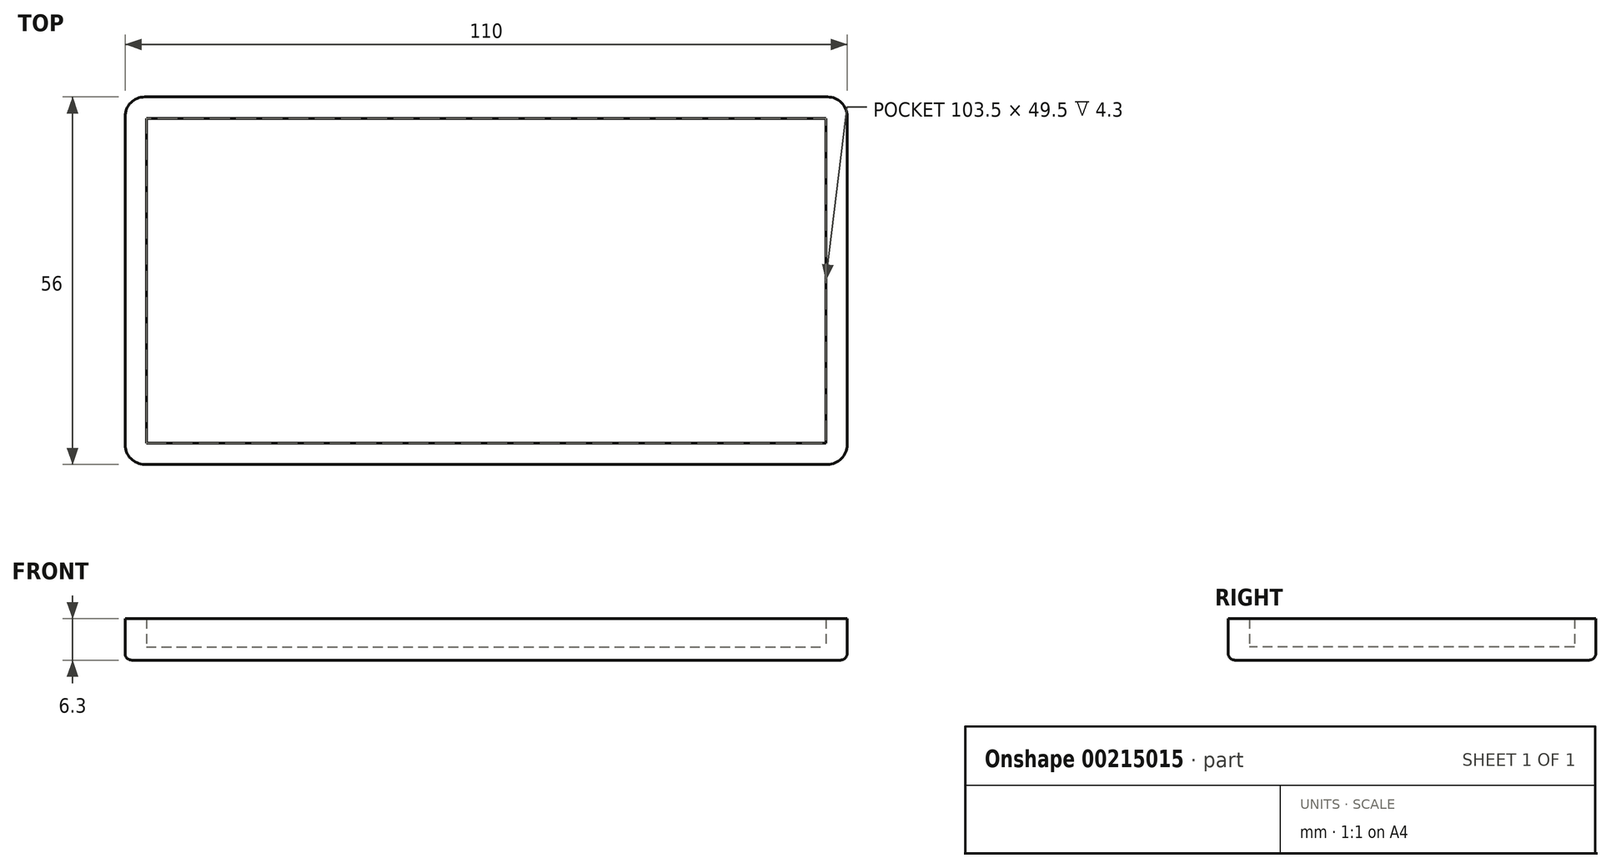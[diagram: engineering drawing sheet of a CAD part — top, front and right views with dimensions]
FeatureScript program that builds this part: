
annotation { "Feature Type Name" : "Feature", "Feature Type Description" : "" }
export const myFeature = defineFeature(function(context is Context, id is Id, definition is map)
    precondition{}
    {
        {
            assignVariable(context, id + "F0", {"name" : "SpessorePiano", "anyValue" : 2 * mm});
        }
        {
            assignVariable(context, id + "F1", {"name" : "AltezzaBordi", "anyValue" : 4.3 * mm});
        }
        {
            assignVariable(context, id + "F2", {"name" : "RaggiaturaSpigoli", "anyValue" : 3 * mm});
        }
        {
            assignVariable(context, id + "F3", {"name" : "RaggiaturaFacciaPiano", "anyValue" : 1 * mm});
        }
        {
            var Q0;
            Q0=qCreatedBy(makeId("Top.planeOp"),FACE);
            var sketch = newSketch(context, id + "F4", { "sketchPlane" : qUnion([Q0])});
            skLineSegment(sketch, "E0.bottom", {"start": v(-51.75, 24.75) * mm, "end": v(51.75, 24.75) * mm});
            skLineSegment(sketch, "E0.top", {"start": v(-51.75, -24.75) * mm, "end": v(51.75, -24.75) * mm});
            skLineSegment(sketch, "E0.left", {"start": v(-51.75, 24.75) * mm, "end": v(-51.75, -24.75) * mm});
            skLineSegment(sketch, "E0.right", {"start": v(51.75, 24.75) * mm, "end": v(51.75, -24.75) * mm});
            skPoint(sketch, "E0.middle", {"position": v(0, 0) * mm});
            skLineSegment(sketch, "E1.bottom", {"start": v(-55, 28) * mm, "end": v(55, 28) * mm});
            skLineSegment(sketch, "E1.top", {"start": v(-55, -28) * mm, "end": v(55, -28) * mm});
            skLineSegment(sketch, "E1.left", {"start": v(-55, 28) * mm, "end": v(-55, -28) * mm});
            skLineSegment(sketch, "E1.right", {"start": v(55, 28) * mm, "end": v(55, -28) * mm});
            skSolve(sketch);
        }
        {
            var Q0;
            Q0 = qSketchRegion(id + "F4", true);
            var Q1;
            Q1=makeQuery(id+"F4.imprint","IMPRINT",FACE,{"disambiguationData":[TD([[makeQuery(id+"F4.imprint","IMPRINT",EDGE,{"derivedFrom":sQuery(id+"F4.wireOp",EDGE,"E0.bottom")}),-1.0]])]});
            extrude(context, id + "F5", {"entities" : qUnion([Q0, Q1]), "oppositeDirection" : true, "depth" : getVariable(context, 'SpessorePiano')});
        }
        {
            var Q0;
            Q0 = qSketchRegion(id + "F4", true);
            extrude(context, id + "F6", {"entities" : qUnion([Q0]), "operationType" : NewBodyOperationType.ADD, "depth" : getVariable(context, 'AltezzaBordi')});
        }
        {
            var Q0;
            {var subQ0=sQuery(id+"F4.wireOp",EDGE,"E1.left");var subQ1=sQuery(id+"F4.wireOp",EDGE,"E1.top");Q0=makeQuery(id+"F6.boolean.opBoolean","MERGE",EDGE,{"derivedFrom":[makeQuery(id+"F5.opExtrude","SWEPT_EDGE",EDGE,{"disambiguationData":[OSD([subQ1,subQ0])]}),makeQuery(id+"F6.opExtrude","SWEPT_EDGE",EDGE,{"disambiguationData":[OSD([subQ1,subQ0])]})]});}
            var Q1;
            {var subQ0=sQuery(id+"F4.wireOp",EDGE,"E1.right");var subQ1=sQuery(id+"F4.wireOp",EDGE,"E1.top");Q1=makeQuery(id+"F6.boolean.opBoolean","MERGE",EDGE,{"derivedFrom":[makeQuery(id+"F5.opExtrude","SWEPT_EDGE",EDGE,{"disambiguationData":[OSD([subQ1,subQ0])]}),makeQuery(id+"F6.opExtrude","SWEPT_EDGE",EDGE,{"disambiguationData":[OSD([subQ1,subQ0])]})]});}
            var Q2;
            {var subQ0=sQuery(id+"F4.wireOp",EDGE,"E1.right");var subQ1=sQuery(id+"F4.wireOp",EDGE,"E1.bottom");Q2=makeQuery(id+"F6.boolean.opBoolean","MERGE",EDGE,{"derivedFrom":[makeQuery(id+"F5.opExtrude","SWEPT_EDGE",EDGE,{"disambiguationData":[OSD([subQ1,subQ0])]}),makeQuery(id+"F6.opExtrude","SWEPT_EDGE",EDGE,{"disambiguationData":[OSD([subQ1,subQ0])]})]});}
            var Q3;
            {var subQ0=sQuery(id+"F4.wireOp",EDGE,"E1.left");var subQ1=sQuery(id+"F4.wireOp",EDGE,"E1.bottom");Q3=makeQuery(id+"F6.boolean.opBoolean","MERGE",EDGE,{"derivedFrom":[makeQuery(id+"F5.opExtrude","SWEPT_EDGE",EDGE,{"disambiguationData":[OSD([subQ1,subQ0])]}),makeQuery(id+"F6.opExtrude","SWEPT_EDGE",EDGE,{"disambiguationData":[OSD([subQ1,subQ0])]})]});}
            fillet(context, id + "F7", {"entities" : qUnion([Q0, Q1, Q2, Q3]), "radius" : getVariable(context, 'RaggiaturaSpigoli'), "tangentPropagation" : true, "allowEdgeOverflow" : false});
        }
        {
            var Q0;
            Q0=makeQuery(id+"F5.opExtrude","CAP_FACE",FACE,{"disambiguationData":[OSD([sQuery(id+"F4.wireOp",EDGE,"E1.bottom"),sQuery(id+"F4.wireOp",EDGE,"E1.top"),sQuery(id+"F4.wireOp",EDGE,"E1.left"),sQuery(id+"F4.wireOp",EDGE,"E1.right")])],"isStart":false});
            fillet(context, id + "F8", {"entities" : qUnion([Q0]), "radius" : getVariable(context, 'RaggiaturaFacciaPiano'), "tangentPropagation" : true, "allowEdgeOverflow" : false});
        }
    });
